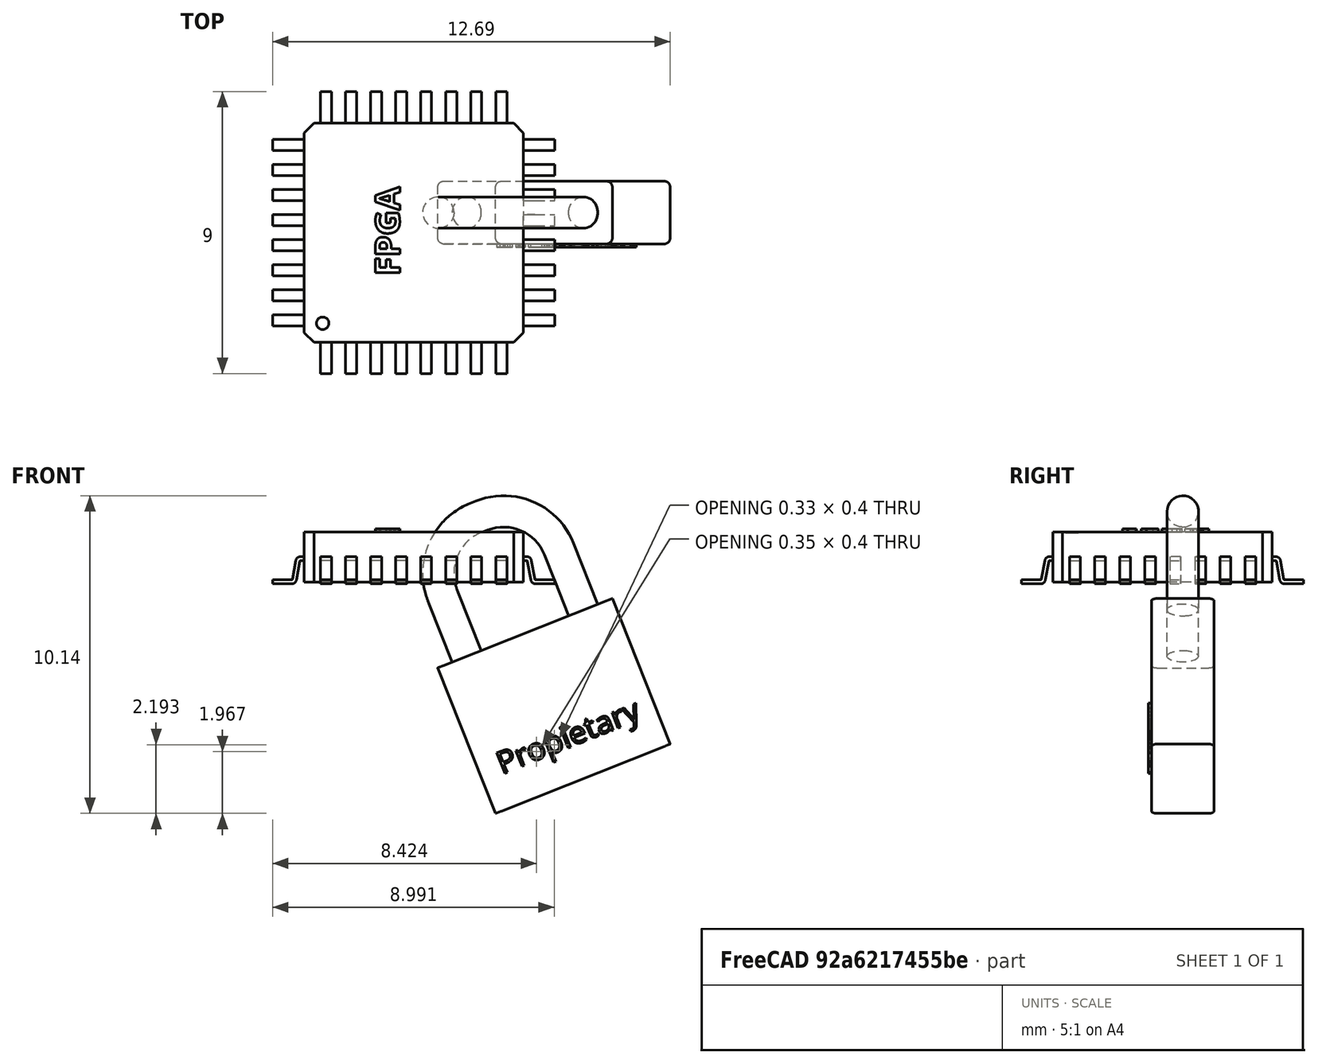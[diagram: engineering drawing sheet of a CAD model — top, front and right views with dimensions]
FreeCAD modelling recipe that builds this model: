
FCSTD DOCUMENT  (FreeCAD 0.16R6703 (Git))
Label: fpga-privative-1
License: CC-BY 3.0
LicenseURL: http://creativecommons.org/licenses/by/3.0/
objects: Part::Part2DObjectPython×5, Part::Extrusion×3, Part::Compound×1, Part::Sweep×1
note: 10 computed .brp shape members not serialized (recipe doc carries the construction recipe); baked Part::Feature solids carry a one-line shape summary decoded from their .brp

FEATURE [Part::Compound] Compound020  label="PQFP-034"
  Placement = pos=(-5.71099,-9.13488,1.7) rot=(0,0,1;0rad)
FEATURE [Part::Part2DObjectPython] DWire  # Draft 2D object (typed FeaturePython)
  ChamferSize = 0
  Closed = false
  End = (2,0,0)
  FilletRadius = 1.9
  Length = 10.369
  MakeFace = true
  Points = (5) [(-2,0,-1.22465e-16),(-2,0,2),(-2,0,4),(2,0,4),(2,0,1.22465e-16)]
  Start = (-2,0,0)
  Subdivisions = 0
FEATURE [Part::Part2DObjectPython] Circle  # Draft 2D object (typed FeaturePython)
  FirstAngle = 0
  LastAngle = 0
  MakeFace = true
  Placement = pos=(-2,0,0) rot=(0,0,1;0rad)
  Radius = 0.5
FEATURE [Part::Sweep] Sweep
  Frenet = true
  Placement = pos=(2.36927,-4,0.070678) rot=(0,-1,0;0.378224rad)
  Sections = -> [Circle]
  Solid = true
  Spine = -> DWire
  Transition = 1
FEATURE [Part::Part2DObjectPython] Rectangle  # Draft 2D object (typed FeaturePython)
  ChamferSize = 0
  Columns = 1
  FilletRadius = 0.2
  Height = -2
  Length = 6
  MakeFace = true
  Placement = pos=(-3,1,0) rot=(0,0,1;0rad)
  Rows = 1
FEATURE [Part::Extrusion] Extrude
  Base = -> Rectangle
  Dir = (0,0,-5)
  Placement = pos=(2.36927,-4,0.070678) rot=(0,-1,0;0.378224rad)
  Solid = true
FEATURE [Part::Part2DObjectPython] ShapeString  # Draft 2D object (typed FeaturePython)
  FontFile = <userpath>/develop/fpgawars.github.io/images/src/Open_Sans/OpenSans-Bold.ttf
  Placement = pos=(-9.34532,3.35513,3.3) rot=(0,0,1;0rad)
  Size = 1
  String = FPGA
  Tracking = 0
FEATURE [Part::Extrusion] Extrude001
  Base = -> ShapeString
  Dir = (0,0,0.1)
  Placement = pos=(1.72771,3.32716,0) rot=(0,0,1;1.5708rad)
  Solid = true
FEATURE [Part::Part2DObjectPython] ShapeString001  # Draft 2D object (typed FeaturePython)
  FontFile = <userpath>/develop/myslides/2016-09-24-Mini-maker-faire-madrid/images/src/Open_Sans/OpenSans-Regular.ttf
  Placement = pos=(1.83581,-5,-4.30397) rot=(0.965264,-0.184751,0.184751;1.60614rad)
  Size = 0.9
  String = Propietary
  Support = -> Extrude
  Tracking = 0
FEATURE [Part::Extrusion] Extrude002
  Base = -> ShapeString001
  Dir = (0,-0.1,0)
  Placement = pos=(-0.201654,0,-0.134656) rot=(0,0,1;0rad)
  Solid = true
